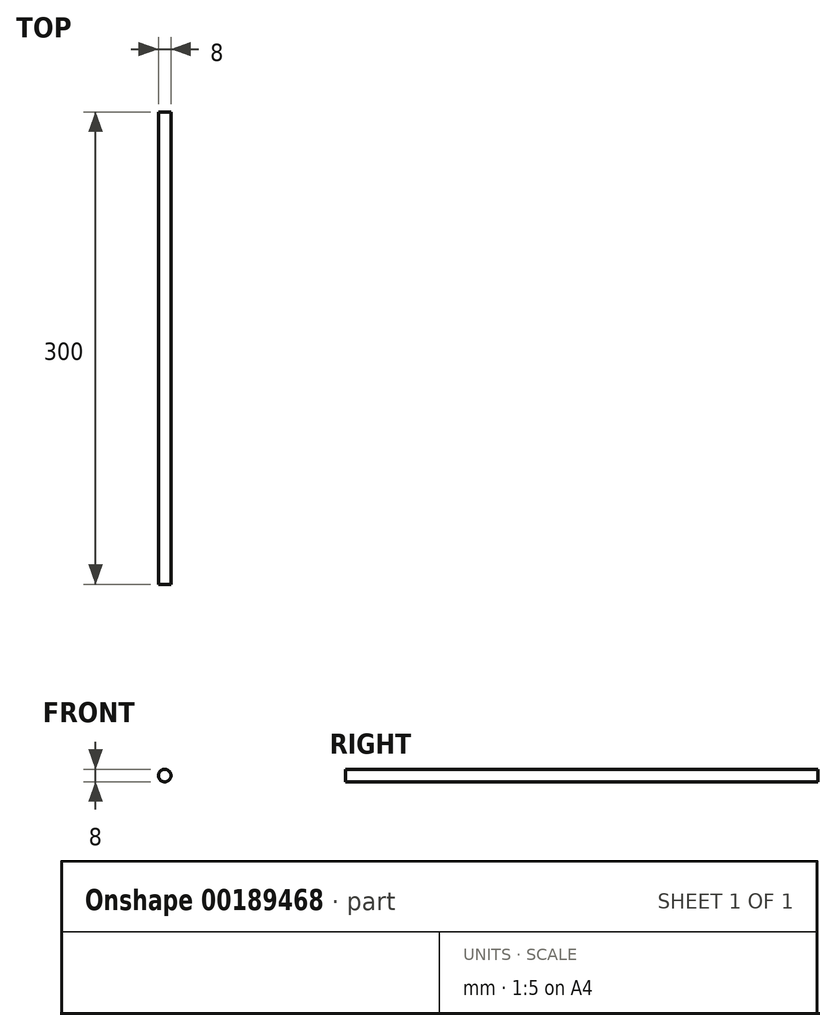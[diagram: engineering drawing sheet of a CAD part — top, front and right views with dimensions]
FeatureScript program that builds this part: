
annotation { "Feature Type Name" : "Feature", "Feature Type Description" : "" }
export const myFeature = defineFeature(function(context is Context, id is Id, definition is map)
    precondition{}
    {
        {
            var Q0;
            Q0=qCreatedBy(makeId("Front.planeOp"),FACE);
            var sketch = newSketch(context, id + "F0", { "sketchPlane" : qUnion([Q0])});
            skCircle(sketch, "E0", {"center": v(0, 0) * mm, "radius": 4 * mm});
            skSolve(sketch);
        }
        {
            var Q0;
            Q0=makeQuery(id+"F0.imprint","IMPRINT",FACE,{"disambiguationData":[TD([[makeQuery(id+"F0.imprint","IMPRINT",EDGE,{"derivedFrom":sQuery(id+"F0.wireOp",EDGE,"E0")}),1.0]])]});
            extrude(context, id + "F1", {"entities" : qUnion([Q0]), "depth" : 300 * mm});
        }
    });
